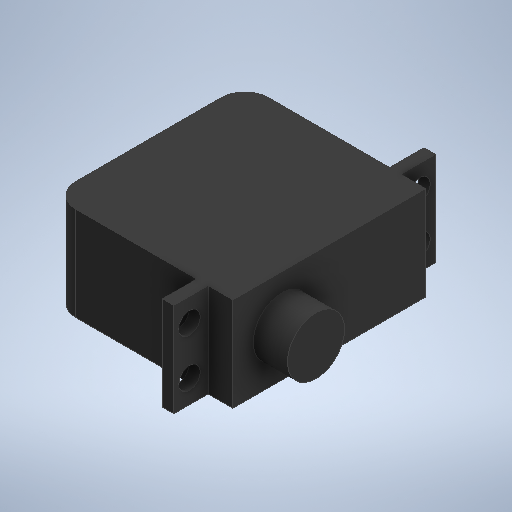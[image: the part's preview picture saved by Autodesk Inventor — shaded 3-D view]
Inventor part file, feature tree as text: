
AUTODESK INVENTOR PART (.ipt)
format: ipt  version: 2025 (Build 290162000, 162)  size: 285,184 bytes
history: native  units: mm
features: extrude x5, sketch x5, fillet x1
ambient origin geometry x8: Origin, YZ Plane, XZ Plane, XY Plane, X Axis, Y Axis, Z Axis, Center Point
bodies: Solide1 (feature_tree)
feature tree (11):
  extrude  "Extrusion1"  Depth=19.7mm
  extrude  "Extrusion2"  Depth=40.5mm
  extrude  "Extrusion3"  Depth=38.0mm TaperAngle=0.0deg
  extrude  "Extrusion4"  Depth=5.2mm
  extrude  "Extrusion5"  Depth=2.4mm
  fillet  "Congé1"  Radius=7.2mm
  sketch  "Esquisse1"
  sketch  "Esquisse2"
  sketch  "Esquisse3"
  sketch  "Esquisse4"
  sketch  "Esquisse5"
